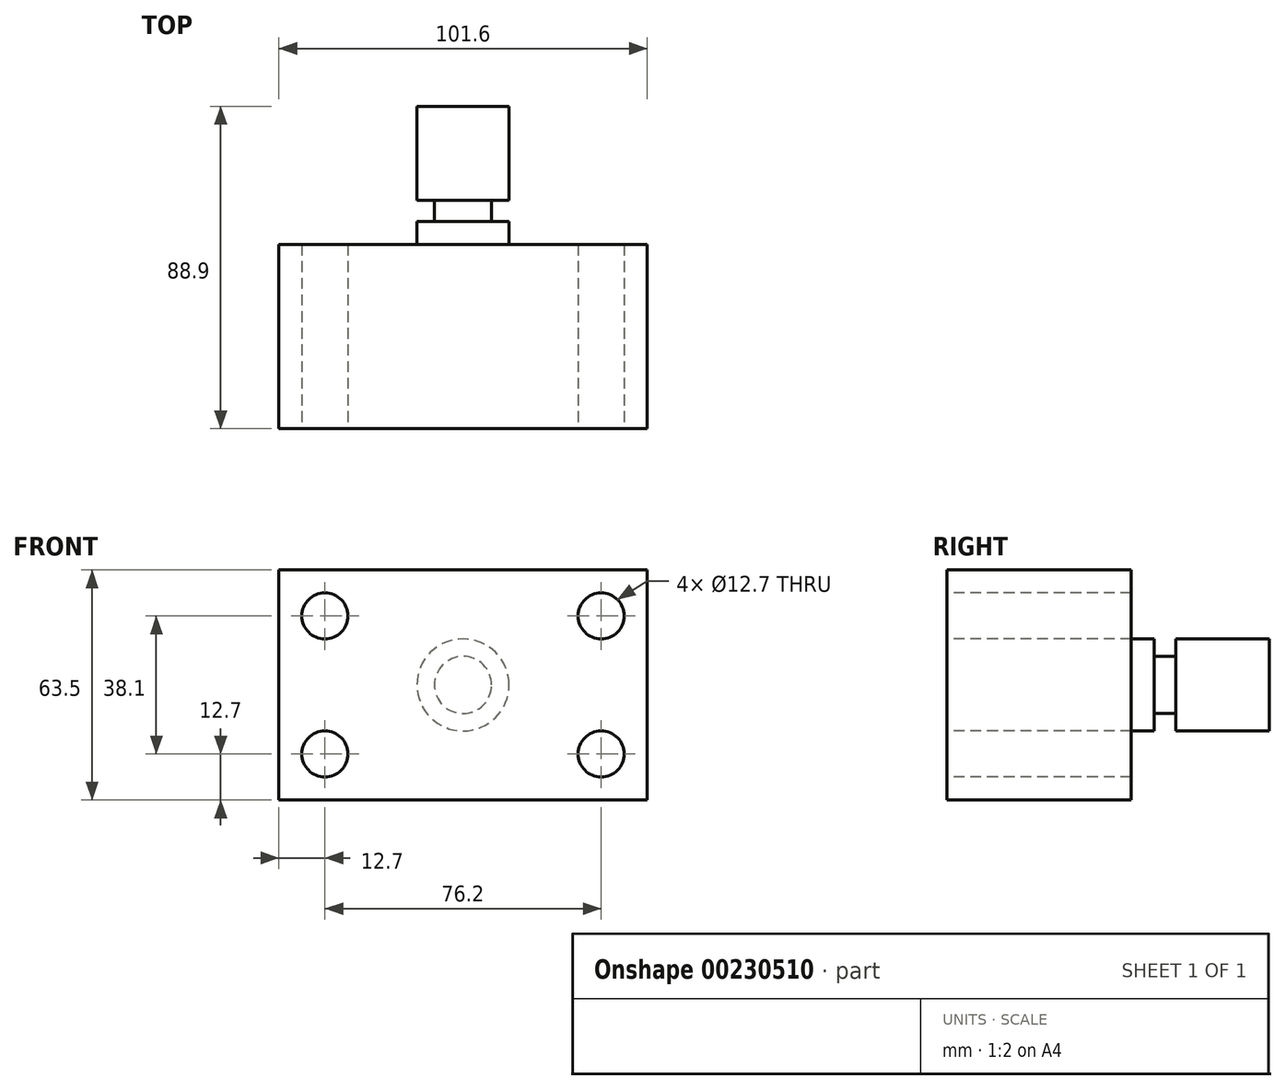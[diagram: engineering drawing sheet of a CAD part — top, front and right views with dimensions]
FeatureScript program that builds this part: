
annotation { "Feature Type Name" : "Feature", "Feature Type Description" : "" }
export const myFeature = defineFeature(function(context is Context, id is Id, definition is map)
    precondition{}
    {
        {
            var Q0;
            Q0=qCreatedBy(makeId("Front.planeOp"),FACE);
            var sketch = newSketch(context, id + "F0", { "sketchPlane" : qUnion([Q0])});
            skLineSegment(sketch, "E0.bottom", {"start": v(-50.8, 31.75) * mm, "end": v(50.8, 31.75) * mm});
            skLineSegment(sketch, "E0.top", {"start": v(-50.8, -31.75) * mm, "end": v(50.8, -31.75) * mm});
            skLineSegment(sketch, "E0.left", {"start": v(-50.8, 31.75) * mm, "end": v(-50.8, -31.75) * mm});
            skLineSegment(sketch, "E0.right", {"start": v(50.8, 31.75) * mm, "end": v(50.8, -31.75) * mm});
            skPoint(sketch, "E0.middle", {"position": v(0, 0) * mm});
            skSolve(sketch);
        }
        {
            var Q0;
            Q0=makeQuery(id+"F0.imprint","IMPRINT",FACE,{"disambiguationData":[TD([[makeQuery(id+"F0.imprint","IMPRINT",EDGE,{"derivedFrom":sQuery(id+"F0.wireOp",EDGE,"E0.bottom")}),-1.0]])]});
            extrude(context, id + "F1", {"entities" : qUnion([Q0]), "oppositeDirection" : true, "depth" : 50.8 * mm});
        }
        {
            var Q0;
            Q0=makeQuery(id+"F1.opExtrude","CAP_FACE",FACE,{"disambiguationData":[OSD([sQuery(id+"F0.wireOp",EDGE,"E0.bottom"),sQuery(id+"F0.wireOp",EDGE,"E0.top"),sQuery(id+"F0.wireOp",EDGE,"E0.left"),sQuery(id+"F0.wireOp",EDGE,"E0.right")])],"isStart":true});
            var sketch = newSketch(context, id + "F2", { "sketchPlane" : qUnion([Q0])});
            skCircle(sketch, "E1", {"center": v(-38.1, 19.05) * mm, "radius": 6.35 * mm});
            skCircle(sketch, "E2", {"center": v(38.1, 19.05) * mm, "radius": 6.35 * mm});
            skCircle(sketch, "E3", {"center": v(38.1, -19.05) * mm, "radius": 6.35 * mm});
            skCircle(sketch, "E4", {"center": v(-38.1, -19.05) * mm, "radius": 6.35 * mm});
            skSolve(sketch);
        }
        {
            var Q0;
            Q0=makeQuery(id+"F2.imprint","IMPRINT",FACE,{"disambiguationData":[TD([[makeQuery(id+"F2.imprint","IMPRINT",EDGE,{"derivedFrom":sQuery(id+"F2.wireOp",EDGE,"E3")}),1.0]])]});
            var Q1;
            Q1=makeQuery(id+"F2.imprint","IMPRINT",FACE,{"disambiguationData":[TD([[makeQuery(id+"F2.imprint","IMPRINT",EDGE,{"derivedFrom":sQuery(id+"F2.wireOp",EDGE,"E2")}),1.0]])]});
            var Q2;
            Q2=makeQuery(id+"F2.imprint","IMPRINT",FACE,{"disambiguationData":[TD([[makeQuery(id+"F2.imprint","IMPRINT",EDGE,{"derivedFrom":sQuery(id+"F2.wireOp",EDGE,"E1")}),1.0]])]});
            var Q3;
            Q3=makeQuery(id+"F2.imprint","IMPRINT",FACE,{"disambiguationData":[TD([[makeQuery(id+"F2.imprint","IMPRINT",EDGE,{"derivedFrom":sQuery(id+"F2.wireOp",EDGE,"E4")}),1.0]])]});
            extrude(context, id + "F3", {"entities" : qUnion([Q0, Q1, Q2, Q3]), "operationType" : NewBodyOperationType.REMOVE, "endBound" : BoundingType.THROUGH_ALL, "oppositeDirection" : true, "depth" : 12.7 * mm});
        }
        {
            var Q0;
            Q0=qCreatedBy(makeId("Top.planeOp"),FACE);
            var sketch = newSketch(context, id + "F4", { "sketchPlane" : qUnion([Q0])});
            skLineSegment(sketch, "E5.bottom", {"start": v(0, 50.8) * mm, "end": v(12.7, 50.8) * mm});
            skLineSegment(sketch, "E5.top", {"start": v(0, 88.9) * mm, "end": v(12.7, 88.9) * mm});
            skLineSegment(sketch, "E5.left", {"start": v(0, 50.8) * mm, "end": v(0, 88.9) * mm});
            skLineSegment(sketch, "E5.right", {"start": v(12.7, 50.8) * mm, "end": v(12.7, 88.9) * mm});
            skSolve(sketch);
        }
        {
            var Q0;
            Q0=makeQuery(id+"F4.imprint","IMPRINT",FACE,{"disambiguationData":[TD([[makeQuery(id+"F4.imprint","IMPRINT",EDGE,{"derivedFrom":sQuery(id+"F4.wireOp",EDGE,"E5.bottom")}),1.0]])]});
            var Q1;
            Q1=sQuery(id+"F4.wireOp",EDGE,"E5.left");
            revolve(context, id + "F5", {"operationType" : NewBodyOperationType.ADD, "entities" : qUnion([Q0]), "axis" : qUnion([Q1]), "revolveType" : RevolveType.FULL});
        }
        {
            var Q0;
            Q0=qCreatedBy(makeId("Top.planeOp"),FACE);
            var sketch = newSketch(context, id + "F6", { "sketchPlane" : qUnion([Q0])});
            skLineSegment(sketch, "E6.bottom", {"start": v(-7.88, 63) * mm, "end": v(-20.58, 63) * mm});
            skLineSegment(sketch, "E6.top", {"start": v(-7.88, 57.15) * mm, "end": v(-20.58, 57.15) * mm});
            skLineSegment(sketch, "E6.left", {"start": v(-7.88, 63) * mm, "end": v(-7.88, 57.15) * mm});
            skLineSegment(sketch, "E6.right", {"start": v(-20.58, 63) * mm, "end": v(-20.58, 57.15) * mm});
            skSolve(sketch);
        }
        {
            var Q0;
            Q0=makeQuery(id+"F6.imprint","IMPRINT",FACE,{"disambiguationData":[TD([[makeQuery(id+"F6.imprint","IMPRINT",EDGE,{"derivedFrom":sQuery(id+"F6.wireOp",EDGE,"E6.bottom")}),1.0]])]});
            var Q1;
            Q1=makeQuery(id+"F5.opRevolve","SWEPT_EDGE",EDGE,{"disambiguationData":[OSD([sQuery(id+"F4.wireOp",EDGE,"E5.top"),sQuery(id+"F4.wireOp",EDGE,"E5.right")])]});
            revolve(context, id + "F7", {"operationType" : NewBodyOperationType.REMOVE, "entities" : qUnion([Q0]), "axis" : qUnion([Q1]), "revolveType" : RevolveType.FULL, "oppositeDirection" : true});
        }
    });
